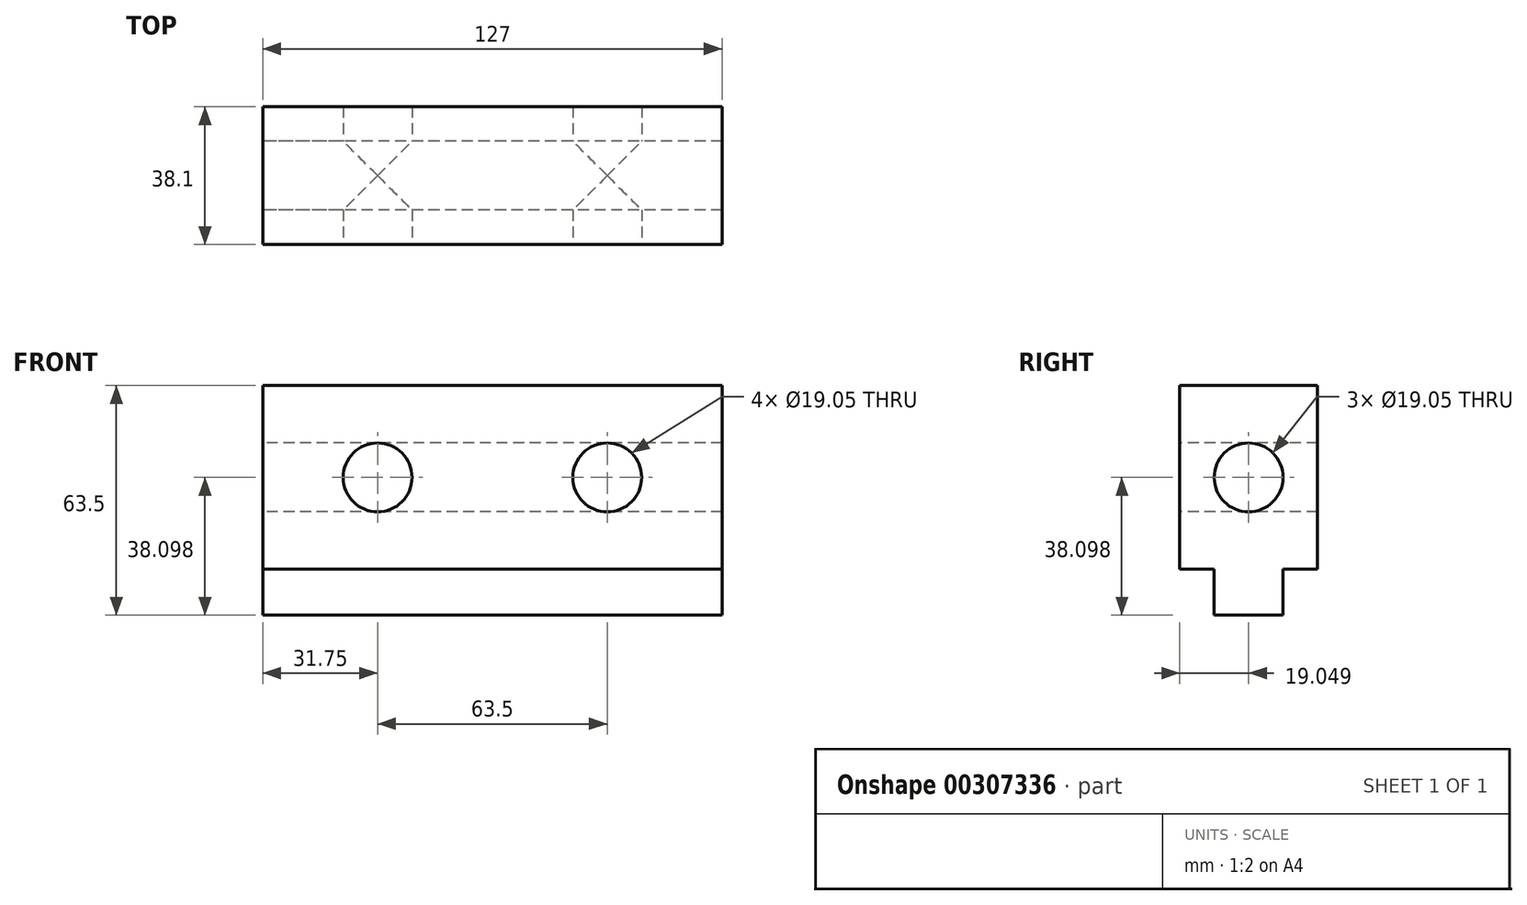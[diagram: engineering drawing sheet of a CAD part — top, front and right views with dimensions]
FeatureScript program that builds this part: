
annotation { "Feature Type Name" : "Feature", "Feature Type Description" : "" }
export const myFeature = defineFeature(function(context is Context, id is Id, definition is map)
    precondition{}
    {
        {
            var Q0;
            Q0=qCreatedBy(makeId("Right.planeOp"),FACE);
            var sketch = newSketch(context, id + "F0", { "sketchPlane" : qUnion([Q0])});
            skLineSegment(sketch, "E0.bottom", {"start": v(-45.64, 12.9) * mm, "end": v(-7.54, 12.9) * mm});
            skLineSegment(sketch, "E0.left", {"start": v(-45.64, 12.9) * mm, "end": v(-45.64, -37.9) * mm});
            skLineSegment(sketch, "E0.right", {"start": v(-7.54, 12.9) * mm, "end": v(-7.54, -37.9) * mm});
            skLineSegment(sketch, "E1", {"start": v(-45.64, -37.9) * mm, "end": v(-36.12, -37.9) * mm});
            skLineSegment(sketch, "E2", {"start": v(-36.12, -37.9) * mm, "end": v(-36.12, -50.6) * mm});
            skLineSegment(sketch, "E3", {"start": v(-36.12, -50.6) * mm, "end": v(-17.07, -50.6) * mm});
            skLineSegment(sketch, "E4", {"start": v(-17.07, -50.6) * mm, "end": v(-17.07, -37.9) * mm});
            skLineSegment(sketch, "E5.trimOffspring", {"start": v(-17.07, -37.9) * mm, "end": v(-7.54, -37.9) * mm});
            skCircle(sketch, "E6", {"center": v(-26.6, -12.5) * mm, "radius": 9.53 * mm});
            skSolve(sketch);
        }
        {
            var Q0;
            Q0=makeQuery(id+"F0.imprint","IMPRINT",FACE,{"disambiguationData":[TD([[makeQuery(id+"F0.imprint","IMPRINT",EDGE,{"derivedFrom":sQuery(id+"F0.wireOp",EDGE,"E0.bottom")}),-1.0]])]});
            extrude(context, id + "F1", {"entities" : qUnion([Q0]), "depth" : 127 * mm});
        }
        {
            var Q0;
            Q0=makeQuery(id+"F1.opExtrude","SWEPT_FACE",FACE,{"disambiguationData":[OSD([sQuery(id+"F0.wireOp",EDGE,"E0.left")])]});
            var sketch = newSketch(context, id + "F2", { "sketchPlane" : qUnion([Q0])});
            skCircle(sketch, "E7", {"center": v(31.75, -12.5) * mm, "radius": 9.53 * mm});
            skCircle(sketch, "E8", {"center": v(95.25, -12.5) * mm, "radius": 9.53 * mm});
            skSolve(sketch);
        }
        {
            var Q0;
            Q0=makeQuery(id+"F2.imprint","IMPRINT",FACE,{"disambiguationData":[TD([[makeQuery(id+"F2.imprint","IMPRINT",EDGE,{"derivedFrom":sQuery(id+"F2.wireOp",EDGE,"E7")}),1.0]])]});
            var Q1;
            Q1=makeQuery(id+"F2.imprint","IMPRINT",FACE,{"disambiguationData":[TD([[makeQuery(id+"F2.imprint","IMPRINT",EDGE,{"derivedFrom":sQuery(id+"F2.wireOp",EDGE,"E8")}),1.0]])]});
            extrude(context, id + "F3", {"entities" : qUnion([Q0, Q1]), "operationType" : NewBodyOperationType.REMOVE, "endBound" : BoundingType.THROUGH_ALL, "oppositeDirection" : true, "depth" : 25.4 * mm});
        }
    });
